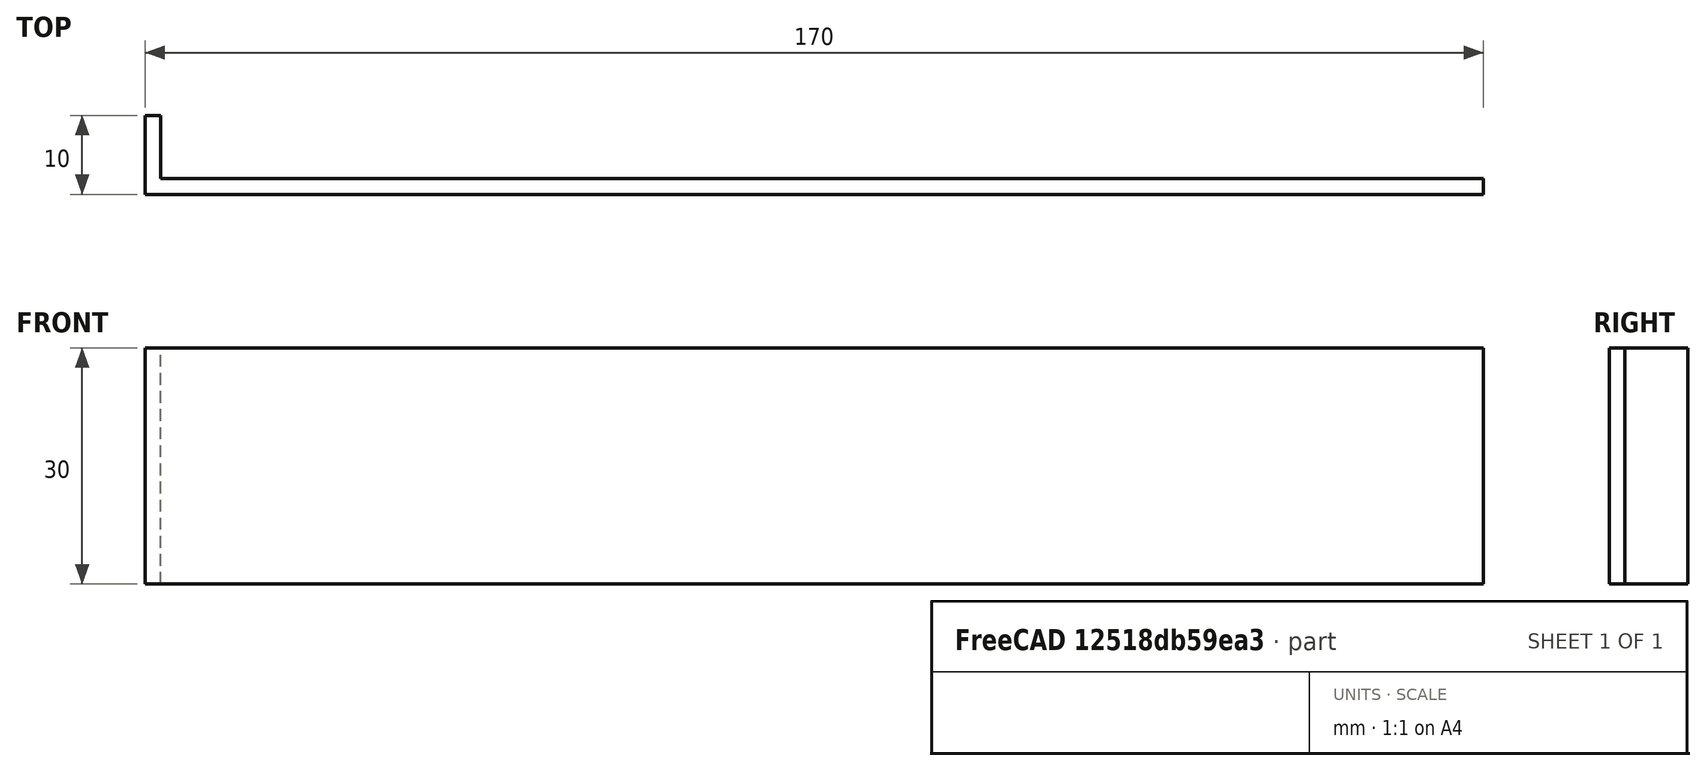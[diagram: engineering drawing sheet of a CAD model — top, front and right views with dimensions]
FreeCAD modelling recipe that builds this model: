
FCSTD DOCUMENT  (FreeCAD 0.20R28671 (Git))
Label: tapa lados
License: All rights reserved
LicenseURL: http://en.wikipedia.org/wiki/All_rights_reserved
objects: TechDraw::DrawViewDimension×6, TechDraw::DrawProjGroupItem×2, Sketcher::SketchObject×1, PartDesign::Pad×1, PartDesign::Body×1, TechDraw::DrawSVGTemplate×1, TechDraw::DrawProjGroup×1, TechDraw::DrawViewSymbol×1, TechDraw::DrawPage×1, TechDraw::DrawViewAnnotation×1
note: 4 computed .brp shape members not serialized (recipe doc carries the construction recipe); baked Part::Feature solids carry a one-line shape summary decoded from their .brp

FEATURE [Sketcher::SketchObject] Sketch
  FullyConstrained = true
  MapMode = 5
  Support = -> [XY_Plane]
  sketch-geometry (7):
    g0: LineSegment StartX=0 StartY=0 StartZ=0 EndX=170 EndY=0 EndZ=0
    g1: LineSegment StartX=0 StartY=0 StartZ=0 EndX=0 EndY=10 EndZ=0
    g2: LineSegment StartX=0 StartY=10 StartZ=0 EndX=2 EndY=10 EndZ=0
    g3: LineSegment StartX=2 StartY=10 StartZ=0 EndX=2 EndY=2 EndZ=0
    g4: LineSegment StartX=2 StartY=2 StartZ=0 EndX=170 EndY=2 EndZ=0
    g5: LineSegment StartX=170 StartY=2 StartZ=0 EndX=170 EndY=0 EndZ=0
    g6: LineSegment StartX=2 StartY=2 StartZ=0 EndX=2 EndY=9e-16 EndZ=0
  constraints (20):
    c: Coincident(g0,g-1)
    c: PointOnObject(g0,g-1)
    c: DistanceX(g0,g0) = 170
    c: Coincident(g1,g0)
    c: PointOnObject(g1,g-2)
    c: Coincident(g2,g1)
    c: Coincident(g3,g2)
    c: Coincident(g4,g3)
    c: Horizontal(g4)
    c: Coincident(g5,g0)
    c: Vertical(g5)
    c: Vertical(g3)
    c: Coincident(g6,g3)
    c: PointOnObject(g6,g0)
    c: Vertical(g6)
    c: Equal(g6,g2)
    c: Horizontal(g2)
    c: DistanceX(g1,g2) = 2
    c: DistanceY(g1,g1) = 10
    c: Coincident(g4,g5)
FEATURE [PartDesign::Pad] Pad
  Direction = (0,0,1)
  Length = 30
  Length2 = 100
  Profile = -> Sketch
  ReferenceAxis = -> Sketch [N_Axis]
  Type = 0
FEATURE [PartDesign::Body] Body
  Group = -> [Sketch,Pad]
  Origin = -> Origin
  Tip = -> Pad
FEATURE [TechDraw::DrawSVGTemplate] Template003
  EditableTexts = AUTHOR_NAME=Daniel García García; DATE=14-04-2022; DN=9; DOCUMENT_TYPE=Plano de pieza; PN=12; REVISION=1; SCALE=1:1; SHEET=9/15; SIZE=A4; TITLELINE-1=Tapa de los lados
  Height = 210
  Orientation = 1
  Width = 297
FEATURE [TechDraw::DrawProjGroupItem] ProjItem  label="Front"
  CoarseView = false
  Direction = (0,-1,0)
  Focus = 100
  HardHidden = false
  IsoCount = 0
  IsoHidden = false
  IsoVisible = false
  LockPosition = true
  Perspective = false
  Rotation = 0
  RotationVector = (1,0,0)
  ScaleType = 2
  SeamHidden = false
  SeamVisible = true
  SmoothHidden = false
  SmoothVisible = true
  Source = -> [Pad]
  Type = 0
  X = 0
  XDirection = (1,0,0)
  Y = 0
FEATURE [TechDraw::DrawProjGroupItem] ProjItem001  label="Top"
  CoarseView = false
  Direction = (0,0,1)
  Focus = 100
  HardHidden = false
  IsoCount = 0
  IsoHidden = false
  IsoVisible = false
  LockPosition = false
  Perspective = false
  Rotation = 0
  RotationVector = (1,0,0)
  ScaleType = 2
  SeamHidden = false
  SeamVisible = true
  SmoothHidden = false
  SmoothVisible = true
  Source = -> [Pad]
  Type = 4
  X = 0
  XDirection = (1,0,0)
  Y = -70.5632
FEATURE [TechDraw::DrawProjGroup] ProjGroup
  Anchor = -> ProjItem
  AutoDistribute = true
  LockPosition = false
  ProjectionType = 0
  Rotation = 0
  ScaleType = 0
  Source = -> [Pad]
  Views = -> [ProjItem,ProjItem001]
  X = 161.357
  Y = 154.821
  spacingX = 15
  spacingY = 15
FEATURE [TechDraw::DrawViewDimension] Dimension
  AngleOverride = false
  Arbitrary = false
  ArbitraryTolerances = false
  EqualTolerance = true
  ExtensionAngle = 0
  FormatSpec = %.2w
  FormatSpecOverTolerance = %+.2w
  FormatSpecUnderTolerance = %+.2w
  Inverted = false
  LineAngle = 0
  LockPosition = false
  MeasureType = 1
  OverTolerance = 0
  References2D = -> [ProjItem]
  Rotation = 0
  ScaleType = 0
  TheoreticalExact = false
  Type = 2
  UnderTolerance = 0
  X = -102.116
  Y = 2.09247
FEATURE [TechDraw::DrawViewDimension] Dimension001
  AngleOverride = false
  Arbitrary = false
  ArbitraryTolerances = false
  EqualTolerance = true
  ExtensionAngle = 0
  FormatSpec = %.2w
  FormatSpecOverTolerance = %+.2w
  FormatSpecUnderTolerance = %+.2w
  Inverted = false
  LineAngle = 0
  LockPosition = false
  MeasureType = 1
  OverTolerance = 0
  References2D = -> [ProjItem001]
  Rotation = 0
  ScaleType = 0
  TheoreticalExact = false
  Type = 1
  UnderTolerance = 0
  X = -1.63013
  Y = 28.767
FEATURE [TechDraw::DrawViewDimension] Dimension002
  AngleOverride = false
  Arbitrary = false
  ArbitraryTolerances = false
  EqualTolerance = true
  ExtensionAngle = 0
  FormatSpec = %.2w
  FormatSpecOverTolerance = %+.2w
  FormatSpecUnderTolerance = %+.2w
  Inverted = false
  LineAngle = 0
  LockPosition = false
  MeasureType = 1
  OverTolerance = 0
  References2D = -> [ProjItem001]
  Rotation = 0
  ScaleType = 0
  TheoreticalExact = false
  Type = 2
  UnderTolerance = 0
  X = -79.5898
  Y = 12.8006
FEATURE [TechDraw::DrawViewDimension] Dimension003
  AngleOverride = false
  Arbitrary = false
  ArbitraryTolerances = false
  EqualTolerance = true
  ExtensionAngle = 0
  FormatSpec = %.2w
  FormatSpecOverTolerance = %+.2w
  FormatSpecUnderTolerance = %+.2w
  Inverted = false
  LineAngle = 0
  LockPosition = false
  MeasureType = 1
  OverTolerance = 0
  References2D = -> [ProjItem001]
  Rotation = 0
  ScaleType = 0
  TheoreticalExact = false
  Type = 2
  UnderTolerance = 0
  X = 90.8904
  Y = 2.22024
FEATURE [TechDraw::DrawViewDimension] Dimension004
  AngleOverride = false
  Arbitrary = false
  ArbitraryTolerances = false
  EqualTolerance = true
  ExtensionAngle = 0
  FormatSpec = %.2w
  FormatSpecOverTolerance = %+.2w
  FormatSpecUnderTolerance = %+.2w
  Inverted = false
  LineAngle = 0
  LockPosition = false
  MeasureType = 1
  OverTolerance = 0
  References2D = -> [ProjItem001]
  Rotation = 0
  ScaleType = 0
  TheoreticalExact = false
  Type = 1
  UnderTolerance = 0
  X = -91.4405
  Y = 21.7609
FEATURE [TechDraw::DrawViewDimension] Dimension005
  AngleOverride = false
  Arbitrary = false
  ArbitraryTolerances = false
  EqualTolerance = true
  ExtensionAngle = 0
  FormatSpec = %.2w
  FormatSpecOverTolerance = %+.2w
  FormatSpecUnderTolerance = %+.2w
  Inverted = false
  LineAngle = 0
  LockPosition = false
  MeasureType = 1
  OverTolerance = 0
  References2D = -> [ProjItem001]
  Rotation = 0
  ScaleType = 0
  TheoreticalExact = false
  Type = 2
  UnderTolerance = 0
  X = -97.7108
  Y = 3.43006
FEATURE [TechDraw::DrawViewSymbol] Symbol
  LockPosition = false
  Rotation = 0
  Scale = 0.3
  ScaleType = 2
  Symbol = <blob: 2444 chars omitted>
  X = 217.487
  Y = 36.9001
FEATURE [TechDraw::DrawPage] Page003  label="Tapa de los lados"
  KeepUpdated = true
  NextBalloonIndex = 1
  ProjectionType = 0
  Template = -> Template003
  Views = -> [ProjGroup,Dimension,Dimension001,Dimension002,Dimension003,Dimension004,Dimension005,Symbol]
FEATURE [TechDraw::DrawViewAnnotation] Annotation
  Font = osifont
  LineSpace = 80
  LockPosition = false
  MaxWidth = -1
  Rotation = 0
  ScaleType = 0
  Text = Default Text
  TextSize = 5
  TextStyle = 0
  X = 148.5
  Y = 105
